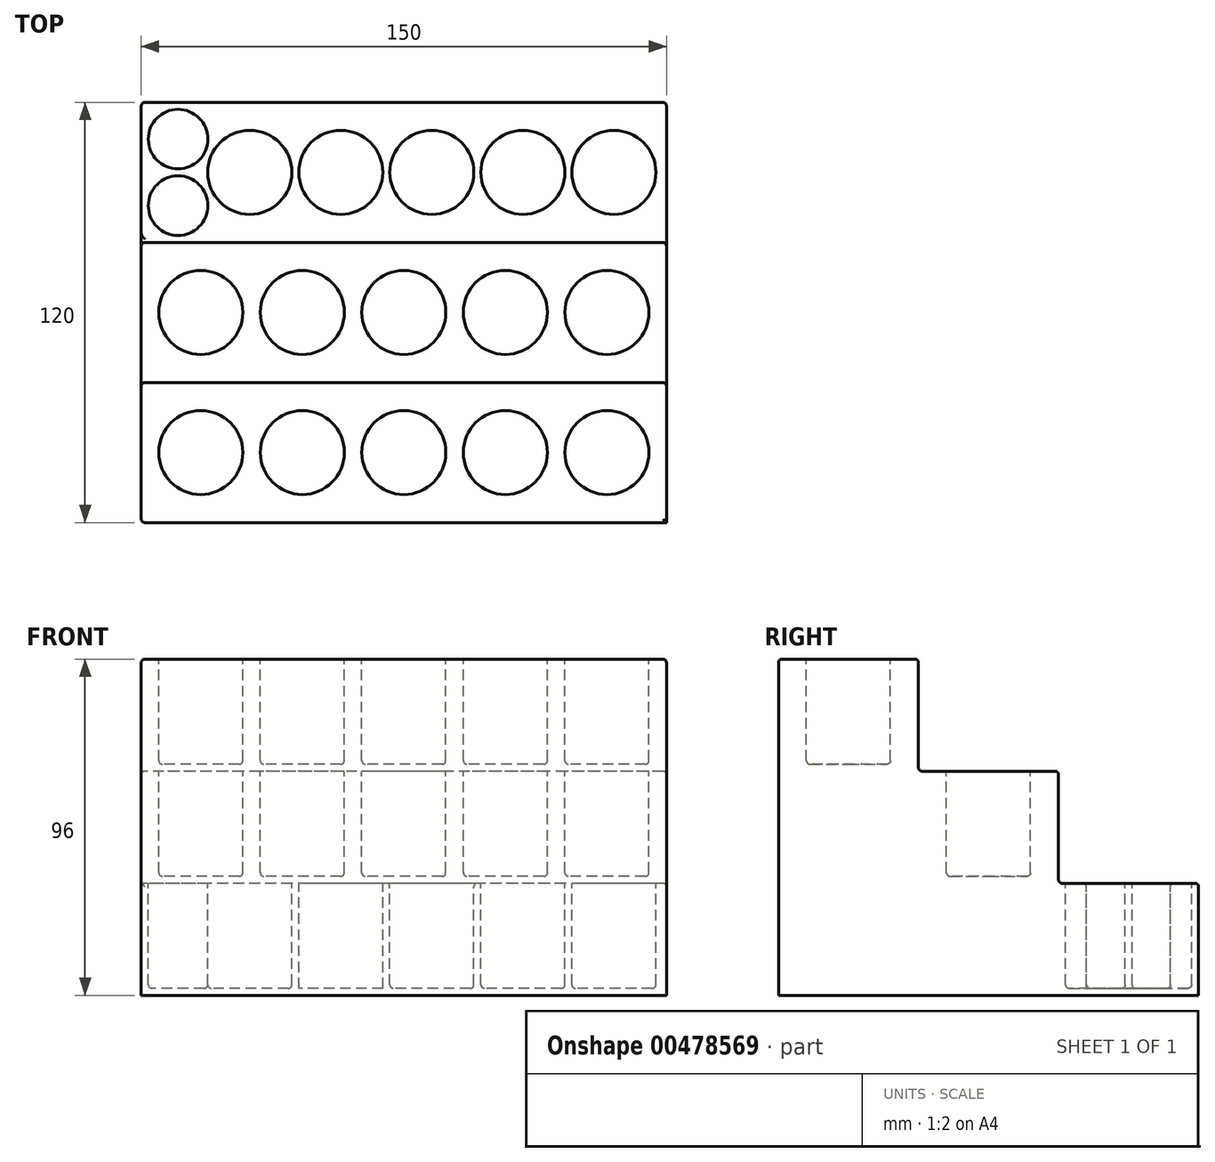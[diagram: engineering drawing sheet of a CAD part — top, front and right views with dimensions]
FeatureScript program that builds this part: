
annotation { "Feature Type Name" : "Feature", "Feature Type Description" : "" }
export const myFeature = defineFeature(function(context is Context, id is Id, definition is map)
    precondition{}
    {
        {
            var Q0;
            Q0=qCreatedBy(makeId("Right.planeOp"),FACE);
            var sketch = newSketch(context, id + "F0", { "sketchPlane" : qUnion([Q0])});
            skLineSegment(sketch, "E0", {"start": v(0, 0) * mm, "end": v(0, 96) * mm});
            skLineSegment(sketch, "E1", {"start": v(0, 96) * mm, "end": v(40, 96) * mm});
            skLineSegment(sketch, "E2", {"start": v(40, 96) * mm, "end": v(40, 64) * mm});
            skLineSegment(sketch, "E3", {"start": v(40, 64) * mm, "end": v(80, 64) * mm});
            skLineSegment(sketch, "E4", {"start": v(80, 64) * mm, "end": v(80, 32) * mm});
            skLineSegment(sketch, "E5", {"start": v(80, 32) * mm, "end": v(120, 32) * mm});
            skLineSegment(sketch, "E6", {"start": v(120, 32) * mm, "end": v(120, 0) * mm});
            skLineSegment(sketch, "E7", {"start": v(120, 0) * mm, "end": v(0, 0) * mm});
            skSolve(sketch);
        }
        {
            var Q0;
            Q0=makeQuery(id+"F0.imprint","IMPRINT",FACE,{"disambiguationData":[TD([[makeQuery(id+"F0.imprint","IMPRINT",EDGE,{"derivedFrom":sQuery(id+"F0.wireOp",EDGE,"E0")}),-1.0]])]});
            extrude(context, id + "F1", {"entities" : qUnion([Q0]), "depth" : 150 * mm});
        }
        {
            var Q0;
            Q0=makeQuery(id+"F1.opExtrude","SWEPT_FACE",FACE,{"disambiguationData":[OSD([sQuery(id+"F0.wireOp",EDGE,"E1")])]});
            var sketch = newSketch(context, id + "F2", { "sketchPlane" : qUnion([Q0])});
            skCircle(sketch, "E8", {"center": v(133, 20) * mm, "radius": 12 * mm});
            skCircle(sketch, "E9.1.0.0", {"center": v(104, 20) * mm, "radius": 12 * mm});
            skCircle(sketch, "E9.2.0.0", {"center": v(75, 20) * mm, "radius": 12 * mm});
            skCircle(sketch, "E9.3.0.0", {"center": v(46, 20) * mm, "radius": 12 * mm});
            skCircle(sketch, "E9.4.0.0", {"center": v(17, 20) * mm, "radius": 12 * mm});
            skLineSegment(sketch, "E9.direction1", {"start": v(133, 20) * mm, "end": v(104, 20) * mm, "construction": true});
            skSolve(sketch);
        }
        {
            var Q0;
            Q0=makeQuery(id+"F1.opExtrude","SWEPT_FACE",FACE,{"disambiguationData":[OSD([sQuery(id+"F0.wireOp",EDGE,"E3")])]});
            var sketch = newSketch(context, id + "F3", { "sketchPlane" : qUnion([Q0])});
            skCircle(sketch, "E10", {"center": v(133, 60) * mm, "radius": 12 * mm});
            skCircle(sketch, "E11.1.0.0", {"center": v(104, 60) * mm, "radius": 12 * mm});
            skCircle(sketch, "E11.2.0.0", {"center": v(75, 60) * mm, "radius": 12 * mm});
            skCircle(sketch, "E11.3.0.0", {"center": v(46, 60) * mm, "radius": 12 * mm});
            skCircle(sketch, "E11.4.0.0", {"center": v(17, 60) * mm, "radius": 12 * mm});
            skLineSegment(sketch, "E11.direction1", {"start": v(133, 60) * mm, "end": v(104, 60) * mm, "construction": true});
            skSolve(sketch);
        }
        {
            var Q0;
            Q0=makeQuery(id+"F2.imprint","IMPRINT",FACE,{"disambiguationData":[TD([[makeQuery(id+"F2.imprint","IMPRINT",EDGE,{"derivedFrom":sQuery(id+"F2.wireOp",EDGE,"E8")}),1.0]])]});
            var Q1;
            Q1=makeQuery(id+"F2.imprint","IMPRINT",FACE,{"disambiguationData":[TD([[makeQuery(id+"F2.imprint","IMPRINT",EDGE,{"derivedFrom":sQuery(id+"F2.wireOp",EDGE,"E9.1.0.0")}),1.0]])]});
            var Q2;
            Q2=makeQuery(id+"F2.imprint","IMPRINT",FACE,{"disambiguationData":[TD([[makeQuery(id+"F2.imprint","IMPRINT",EDGE,{"derivedFrom":sQuery(id+"F2.wireOp",EDGE,"E9.2.0.0")}),1.0]])]});
            var Q3;
            Q3=makeQuery(id+"F2.imprint","IMPRINT",FACE,{"disambiguationData":[TD([[makeQuery(id+"F2.imprint","IMPRINT",EDGE,{"derivedFrom":sQuery(id+"F2.wireOp",EDGE,"E9.3.0.0")}),1.0]])]});
            var Q4;
            Q4=makeQuery(id+"F2.imprint","IMPRINT",FACE,{"disambiguationData":[TD([[makeQuery(id+"F2.imprint","IMPRINT",EDGE,{"derivedFrom":sQuery(id+"F2.wireOp",EDGE,"E9.4.0.0")}),1.0]])]});
            var Q5;
            Q5=makeQuery(id+"F3.imprint","IMPRINT",FACE,{"disambiguationData":[TD([[makeQuery(id+"F3.imprint","IMPRINT",EDGE,{"derivedFrom":sQuery(id+"F3.wireOp",EDGE,"E11.4.0.0")}),1.0]])]});
            var Q6;
            Q6=makeQuery(id+"F3.imprint","IMPRINT",FACE,{"disambiguationData":[TD([[makeQuery(id+"F3.imprint","IMPRINT",EDGE,{"derivedFrom":sQuery(id+"F3.wireOp",EDGE,"E11.3.0.0")}),1.0]])]});
            var Q7;
            Q7=makeQuery(id+"F3.imprint","IMPRINT",FACE,{"disambiguationData":[TD([[makeQuery(id+"F3.imprint","IMPRINT",EDGE,{"derivedFrom":sQuery(id+"F3.wireOp",EDGE,"E11.2.0.0")}),1.0]])]});
            var Q8;
            Q8=makeQuery(id+"F3.imprint","IMPRINT",FACE,{"disambiguationData":[TD([[makeQuery(id+"F3.imprint","IMPRINT",EDGE,{"derivedFrom":sQuery(id+"F3.wireOp",EDGE,"E11.1.0.0")}),1.0]])]});
            var Q9;
            Q9=makeQuery(id+"F3.imprint","IMPRINT",FACE,{"disambiguationData":[TD([[makeQuery(id+"F3.imprint","IMPRINT",EDGE,{"derivedFrom":sQuery(id+"F3.wireOp",EDGE,"E10")}),1.0]])]});
            extrude(context, id + "F4", {"entities" : qUnion([Q0, Q1, Q2, Q3, Q4, Q5, Q6, Q7, Q8, Q9]), "operationType" : NewBodyOperationType.REMOVE, "oppositeDirection" : true, "depth" : 30 * mm});
        }
        {
            var Q0;
            Q0=makeQuery(id+"F1.opExtrude","SWEPT_FACE",FACE,{"disambiguationData":[OSD([sQuery(id+"F0.wireOp",EDGE,"E5")])]});
            var sketch = newSketch(context, id + "F5", { "sketchPlane" : qUnion([Q0])});
            skCircle(sketch, "E12", {"center": v(135, 100) * mm, "radius": 12 * mm});
            skCircle(sketch, "E13.1.0.0", {"center": v(109, 100) * mm, "radius": 12 * mm});
            skCircle(sketch, "E13.2.0.0", {"center": v(83, 100) * mm, "radius": 12 * mm});
            skCircle(sketch, "E13.3.0.0", {"center": v(57, 100) * mm, "radius": 12 * mm});
            skCircle(sketch, "E13.4.0.0", {"center": v(31, 100) * mm, "radius": 12 * mm});
            skLineSegment(sketch, "E13.direction1", {"start": v(135, 100) * mm, "end": v(109, 100) * mm, "construction": true});
            skCircle(sketch, "E14", {"center": v(10.5, 90.5) * mm, "radius": 8.5 * mm});
            skCircle(sketch, "E15", {"center": v(10.5, 109.5) * mm, "radius": 8.5 * mm});
            skSolve(sketch);
        }
        {
            var Q0;
            Q0=makeQuery(id+"F5.imprint","IMPRINT",FACE,{"disambiguationData":[TD([[makeQuery(id+"F5.imprint","IMPRINT",EDGE,{"derivedFrom":sQuery(id+"F5.wireOp",EDGE,"E12")}),1.0]])]});
            var Q1;
            Q1=makeQuery(id+"F5.imprint","IMPRINT",FACE,{"disambiguationData":[TD([[makeQuery(id+"F5.imprint","IMPRINT",EDGE,{"derivedFrom":sQuery(id+"F5.wireOp",EDGE,"E13.1.0.0")}),1.0]])]});
            var Q2;
            Q2=makeQuery(id+"F5.imprint","IMPRINT",FACE,{"disambiguationData":[TD([[makeQuery(id+"F5.imprint","IMPRINT",EDGE,{"derivedFrom":sQuery(id+"F5.wireOp",EDGE,"E13.2.0.0")}),1.0]])]});
            var Q3;
            Q3=makeQuery(id+"F5.imprint","IMPRINT",FACE,{"disambiguationData":[TD([[makeQuery(id+"F5.imprint","IMPRINT",EDGE,{"derivedFrom":sQuery(id+"F5.wireOp",EDGE,"E13.3.0.0")}),1.0]])]});
            var Q4;
            Q4=makeQuery(id+"F5.imprint","IMPRINT",FACE,{"disambiguationData":[TD([[makeQuery(id+"F5.imprint","IMPRINT",EDGE,{"derivedFrom":sQuery(id+"F5.wireOp",EDGE,"E13.4.0.0")}),1.0]])]});
            var Q5;
            Q5=makeQuery(id+"F5.imprint","IMPRINT",FACE,{"disambiguationData":[TD([[makeQuery(id+"F5.imprint","IMPRINT",EDGE,{"derivedFrom":sQuery(id+"F5.wireOp",EDGE,"E14")}),1.0]])]});
            var Q6;
            Q6=makeQuery(id+"F5.imprint","IMPRINT",FACE,{"disambiguationData":[TD([[makeQuery(id+"F5.imprint","IMPRINT",EDGE,{"derivedFrom":sQuery(id+"F5.wireOp",EDGE,"E15")}),1.0]])]});
            extrude(context, id + "F6", {"entities" : qUnion([Q0, Q1, Q2, Q3, Q4, Q5, Q6]), "operationType" : NewBodyOperationType.REMOVE, "oppositeDirection" : true, "depth" : 30 * mm});
        }
        {
            var Q0;
            Q0=makeQuery(id+"F1.opExtrude","SWEPT_EDGE",EDGE,{"disambiguationData":[OSD([sQuery(id+"F0.wireOp",EDGE,"E0"),sQuery(id+"F0.wireOp",EDGE,"E1")])]});
            var Q1;
            Q1=makeQuery(id+"F1.opExtrude","CAP_EDGE",EDGE,{"disambiguationData":[OSD([sQuery(id+"F0.wireOp",EDGE,"E1")])],"isStart":false});
            var Q2;
            Q2=makeQuery(id+"F1.opExtrude","SWEPT_EDGE",EDGE,{"disambiguationData":[OSD([sQuery(id+"F0.wireOp",EDGE,"E1"),sQuery(id+"F0.wireOp",EDGE,"E2")])]});
            var Q3;
            Q3=makeQuery(id+"F1.opExtrude","CAP_EDGE",EDGE,{"disambiguationData":[OSD([sQuery(id+"F0.wireOp",EDGE,"E1")])],"isStart":true});
            var Q4;
            Q4=makeQuery(id+"F4.boolean.opBoolean","COPY",EDGE,{"derivedFrom":makeQuery(id+"F4.opExtrude","CAP_EDGE",EDGE,{"disambiguationData":[OSD([sQuery(id+"F2.wireOp",EDGE,"E9.4.0.0")])],"isStart":true})});
            var Q5;
            Q5=makeQuery(id+"F4.boolean.opBoolean","COPY",EDGE,{"derivedFrom":makeQuery(id+"F4.opExtrude","CAP_EDGE",EDGE,{"disambiguationData":[OSD([sQuery(id+"F2.wireOp",EDGE,"E9.3.0.0")])],"isStart":true})});
            var Q6;
            Q6=makeQuery(id+"F4.boolean.opBoolean","COPY",EDGE,{"derivedFrom":makeQuery(id+"F4.opExtrude","CAP_EDGE",EDGE,{"disambiguationData":[OSD([sQuery(id+"F2.wireOp",EDGE,"E9.2.0.0")])],"isStart":true})});
            var Q7;
            Q7=makeQuery(id+"F4.boolean.opBoolean","COPY",EDGE,{"derivedFrom":makeQuery(id+"F4.opExtrude","CAP_EDGE",EDGE,{"disambiguationData":[OSD([sQuery(id+"F2.wireOp",EDGE,"E9.1.0.0")])],"isStart":true})});
            var Q8;
            Q8=makeQuery(id+"F4.boolean.opBoolean","COPY",EDGE,{"derivedFrom":makeQuery(id+"F4.opExtrude","CAP_EDGE",EDGE,{"disambiguationData":[OSD([sQuery(id+"F2.wireOp",EDGE,"E8")])],"isStart":true})});
            var Q9;
            Q9=makeQuery(id+"F1.opExtrude","CAP_EDGE",EDGE,{"disambiguationData":[OSD([sQuery(id+"F0.wireOp",EDGE,"E2")])],"isStart":false});
            var Q10;
            Q10=makeQuery(id+"F1.opExtrude","CAP_EDGE",EDGE,{"disambiguationData":[OSD([sQuery(id+"F0.wireOp",EDGE,"E3")])],"isStart":false});
            var Q11;
            Q11=makeQuery(id+"F1.opExtrude","CAP_EDGE",EDGE,{"disambiguationData":[OSD([sQuery(id+"F0.wireOp",EDGE,"E4")])],"isStart":false});
            var Q12;
            Q12=makeQuery(id+"F1.opExtrude","SWEPT_EDGE",EDGE,{"disambiguationData":[OSD([sQuery(id+"F0.wireOp",EDGE,"E3"),sQuery(id+"F0.wireOp",EDGE,"E4")])]});
            var Q13;
            Q13=makeQuery(id+"F1.opExtrude","SWEPT_EDGE",EDGE,{"disambiguationData":[OSD([sQuery(id+"F0.wireOp",EDGE,"E2"),sQuery(id+"F0.wireOp",EDGE,"E3")])]});
            var Q14;
            Q14=makeQuery(id+"F1.opExtrude","CAP_EDGE",EDGE,{"disambiguationData":[OSD([sQuery(id+"F0.wireOp",EDGE,"E2")])],"isStart":true});
            var Q15;
            Q15=makeQuery(id+"F1.opExtrude","CAP_EDGE",EDGE,{"disambiguationData":[OSD([sQuery(id+"F0.wireOp",EDGE,"E3")])],"isStart":true});
            var Q16;
            Q16=makeQuery(id+"F4.boolean.opBoolean","COPY",EDGE,{"derivedFrom":makeQuery(id+"F4.opExtrude","CAP_EDGE",EDGE,{"disambiguationData":[OSD([sQuery(id+"F3.wireOp",EDGE,"E11.4.0.0")])],"isStart":true})});
            var Q17;
            Q17=makeQuery(id+"F4.boolean.opBoolean","COPY",EDGE,{"derivedFrom":makeQuery(id+"F4.opExtrude","CAP_EDGE",EDGE,{"disambiguationData":[OSD([sQuery(id+"F3.wireOp",EDGE,"E11.3.0.0")])],"isStart":true})});
            var Q18;
            Q18=makeQuery(id+"F4.boolean.opBoolean","COPY",EDGE,{"derivedFrom":makeQuery(id+"F4.opExtrude","CAP_EDGE",EDGE,{"disambiguationData":[OSD([sQuery(id+"F3.wireOp",EDGE,"E11.2.0.0")])],"isStart":true})});
            var Q19;
            Q19=makeQuery(id+"F4.boolean.opBoolean","COPY",EDGE,{"derivedFrom":makeQuery(id+"F4.opExtrude","CAP_EDGE",EDGE,{"disambiguationData":[OSD([sQuery(id+"F3.wireOp",EDGE,"E11.1.0.0")])],"isStart":true})});
            var Q20;
            Q20=makeQuery(id+"F4.boolean.opBoolean","COPY",EDGE,{"derivedFrom":makeQuery(id+"F4.opExtrude","CAP_EDGE",EDGE,{"disambiguationData":[OSD([sQuery(id+"F3.wireOp",EDGE,"E10")])],"isStart":true})});
            var Q21;
            Q21=makeQuery(id+"F1.opExtrude","CAP_EDGE",EDGE,{"disambiguationData":[OSD([sQuery(id+"F0.wireOp",EDGE,"E4")])],"isStart":true});
            var Q22;
            Q22=makeQuery(id+"F1.opExtrude","CAP_EDGE",EDGE,{"disambiguationData":[OSD([sQuery(id+"F0.wireOp",EDGE,"E0")])],"isStart":true});
            var Q23;
            Q23=makeQuery(id+"F1.opExtrude","CAP_EDGE",EDGE,{"disambiguationData":[OSD([sQuery(id+"F0.wireOp",EDGE,"E6")])],"isStart":true});
            var Q24;
            Q24=makeQuery(id+"F1.opExtrude","CAP_EDGE",EDGE,{"disambiguationData":[OSD([sQuery(id+"F0.wireOp",EDGE,"E6")])],"isStart":false});
            var Q25;
            Q25=makeQuery(id+"F1.opExtrude","CAP_EDGE",EDGE,{"disambiguationData":[OSD([sQuery(id+"F0.wireOp",EDGE,"E5")])],"isStart":false});
            var Q26;
            Q26=makeQuery(id+"F1.opExtrude","SWEPT_EDGE",EDGE,{"disambiguationData":[OSD([sQuery(id+"F0.wireOp",EDGE,"E4"),sQuery(id+"F0.wireOp",EDGE,"E5")])]});
            var Q27;
            Q27=makeQuery(id+"F6.boolean.opBoolean","COPY",EDGE,{"derivedFrom":makeQuery(id+"F6.opExtrude","CAP_EDGE",EDGE,{"disambiguationData":[OSD([sQuery(id+"F5.wireOp",EDGE,"E12")])],"isStart":true})});
            var Q28;
            Q28=makeQuery(id+"F6.boolean.opBoolean","COPY",EDGE,{"derivedFrom":makeQuery(id+"F6.opExtrude","CAP_EDGE",EDGE,{"disambiguationData":[OSD([sQuery(id+"F5.wireOp",EDGE,"E13.1.0.0")])],"isStart":true})});
            var Q29;
            Q29=makeQuery(id+"F6.boolean.opBoolean","COPY",FACE,{"derivedFrom":makeQuery(id+"F6.opExtrude","SWEPT_FACE",FACE,{"disambiguationData":[OSD([sQuery(id+"F5.wireOp",EDGE,"E13.2.0.0")])]})});
            var Q30;
            Q30=makeQuery(id+"F1.opExtrude","SWEPT_EDGE",EDGE,{"disambiguationData":[OSD([sQuery(id+"F0.wireOp",EDGE,"E5"),sQuery(id+"F0.wireOp",EDGE,"E6")])]});
            var Q31;
            Q31=makeQuery(id+"F6.boolean.opBoolean","COPY",EDGE,{"derivedFrom":makeQuery(id+"F6.opExtrude","CAP_EDGE",EDGE,{"disambiguationData":[OSD([sQuery(id+"F5.wireOp",EDGE,"E13.3.0.0")])],"isStart":true})});
            var Q32;
            Q32=makeQuery(id+"F6.boolean.opBoolean","COPY",EDGE,{"derivedFrom":makeQuery(id+"F6.opExtrude","CAP_EDGE",EDGE,{"disambiguationData":[OSD([sQuery(id+"F5.wireOp",EDGE,"E13.4.0.0")])],"isStart":true})});
            var Q33;
            Q33=makeQuery(id+"F6.boolean.opBoolean","COPY",EDGE,{"derivedFrom":makeQuery(id+"F6.opExtrude","CAP_EDGE",EDGE,{"disambiguationData":[OSD([sQuery(id+"F5.wireOp",EDGE,"E12")])],"isStart":false})});
            var Q34;
            Q34=makeQuery(id+"F6.boolean.opBoolean","COPY",EDGE,{"derivedFrom":makeQuery(id+"F6.opExtrude","CAP_EDGE",EDGE,{"disambiguationData":[OSD([sQuery(id+"F5.wireOp",EDGE,"E13.1.0.0")])],"isStart":false})});
            var Q35;
            Q35=makeQuery(id+"F6.boolean.opBoolean","COPY",EDGE,{"derivedFrom":makeQuery(id+"F6.opExtrude","CAP_EDGE",EDGE,{"disambiguationData":[OSD([sQuery(id+"F5.wireOp",EDGE,"E13.4.0.0")])],"isStart":false})});
            var Q36;
            Q36=makeQuery(id+"F6.boolean.opBoolean","COPY",EDGE,{"derivedFrom":makeQuery(id+"F6.opExtrude","CAP_EDGE",EDGE,{"disambiguationData":[OSD([sQuery(id+"F5.wireOp",EDGE,"E14")])],"isStart":false})});
            var Q37;
            Q37=makeQuery(id+"F6.boolean.opBoolean","COPY",EDGE,{"derivedFrom":makeQuery(id+"F6.opExtrude","CAP_EDGE",EDGE,{"disambiguationData":[OSD([sQuery(id+"F5.wireOp",EDGE,"E15")])],"isStart":false})});
            var Q38;
            Q38=makeQuery(id+"F4.boolean.opBoolean","COPY",FACE,{"derivedFrom":makeQuery(id+"F4.opExtrude","CAP_FACE",FACE,{"disambiguationData":[OSD([sQuery(id+"F3.wireOp",EDGE,"E11.4.0.0")])],"isStart":false})});
            var Q39;
            Q39=makeQuery(id+"F4.boolean.opBoolean","COPY",EDGE,{"derivedFrom":makeQuery(id+"F4.opExtrude","CAP_EDGE",EDGE,{"disambiguationData":[OSD([sQuery(id+"F3.wireOp",EDGE,"E11.3.0.0")])],"isStart":false})});
            var Q40;
            Q40=makeQuery(id+"F4.boolean.opBoolean","COPY",EDGE,{"derivedFrom":makeQuery(id+"F4.opExtrude","CAP_EDGE",EDGE,{"disambiguationData":[OSD([sQuery(id+"F3.wireOp",EDGE,"E11.2.0.0")])],"isStart":false})});
            var Q41;
            Q41=makeQuery(id+"F4.boolean.opBoolean","COPY",EDGE,{"derivedFrom":makeQuery(id+"F4.opExtrude","CAP_EDGE",EDGE,{"disambiguationData":[OSD([sQuery(id+"F3.wireOp",EDGE,"E11.1.0.0")])],"isStart":false})});
            var Q42;
            Q42=makeQuery(id+"F4.boolean.opBoolean","COPY",EDGE,{"derivedFrom":makeQuery(id+"F4.opExtrude","CAP_EDGE",EDGE,{"disambiguationData":[OSD([sQuery(id+"F3.wireOp",EDGE,"E10")])],"isStart":false})});
            var Q43;
            Q43=makeQuery(id+"F4.boolean.opBoolean","COPY",EDGE,{"derivedFrom":makeQuery(id+"F4.opExtrude","CAP_EDGE",EDGE,{"disambiguationData":[OSD([sQuery(id+"F2.wireOp",EDGE,"E9.4.0.0")])],"isStart":false})});
            var Q44;
            Q44=makeQuery(id+"F4.boolean.opBoolean","COPY",FACE,{"derivedFrom":makeQuery(id+"F4.opExtrude","CAP_FACE",FACE,{"disambiguationData":[OSD([sQuery(id+"F2.wireOp",EDGE,"E9.3.0.0")])],"isStart":false})});
            var Q45;
            Q45=makeQuery(id+"F4.boolean.opBoolean","COPY",FACE,{"derivedFrom":makeQuery(id+"F4.opExtrude","CAP_FACE",FACE,{"disambiguationData":[OSD([sQuery(id+"F2.wireOp",EDGE,"E9.2.0.0")])],"isStart":false})});
            var Q46;
            Q46=makeQuery(id+"F4.boolean.opBoolean","COPY",EDGE,{"derivedFrom":makeQuery(id+"F4.opExtrude","CAP_EDGE",EDGE,{"disambiguationData":[OSD([sQuery(id+"F2.wireOp",EDGE,"E9.1.0.0")])],"isStart":false})});
            var Q47;
            Q47=makeQuery(id+"F4.boolean.opBoolean","COPY",EDGE,{"derivedFrom":makeQuery(id+"F4.opExtrude","CAP_EDGE",EDGE,{"disambiguationData":[OSD([sQuery(id+"F2.wireOp",EDGE,"E8")])],"isStart":false})});
            fillet(context, id + "F7", {"entities" : qUnion([Q0, Q1, Q2, Q3, Q4, Q5, Q6, Q7, Q8, Q9, Q10, Q11, Q12, Q13, Q14, Q15, Q16, Q17, Q18, Q19, Q20, Q21, Q22, Q23, Q24, Q25, Q26, Q27, Q28, Q29, Q30, Q31, Q32, Q33, Q34, Q35, Q36, Q37, Q38, Q39, Q40, Q41, Q42, Q43, Q44, Q45, Q46, Q47]), "radius" : 1 * mm, "tangentPropagation" : true, "allowEdgeOverflow" : false});
        }
    });
